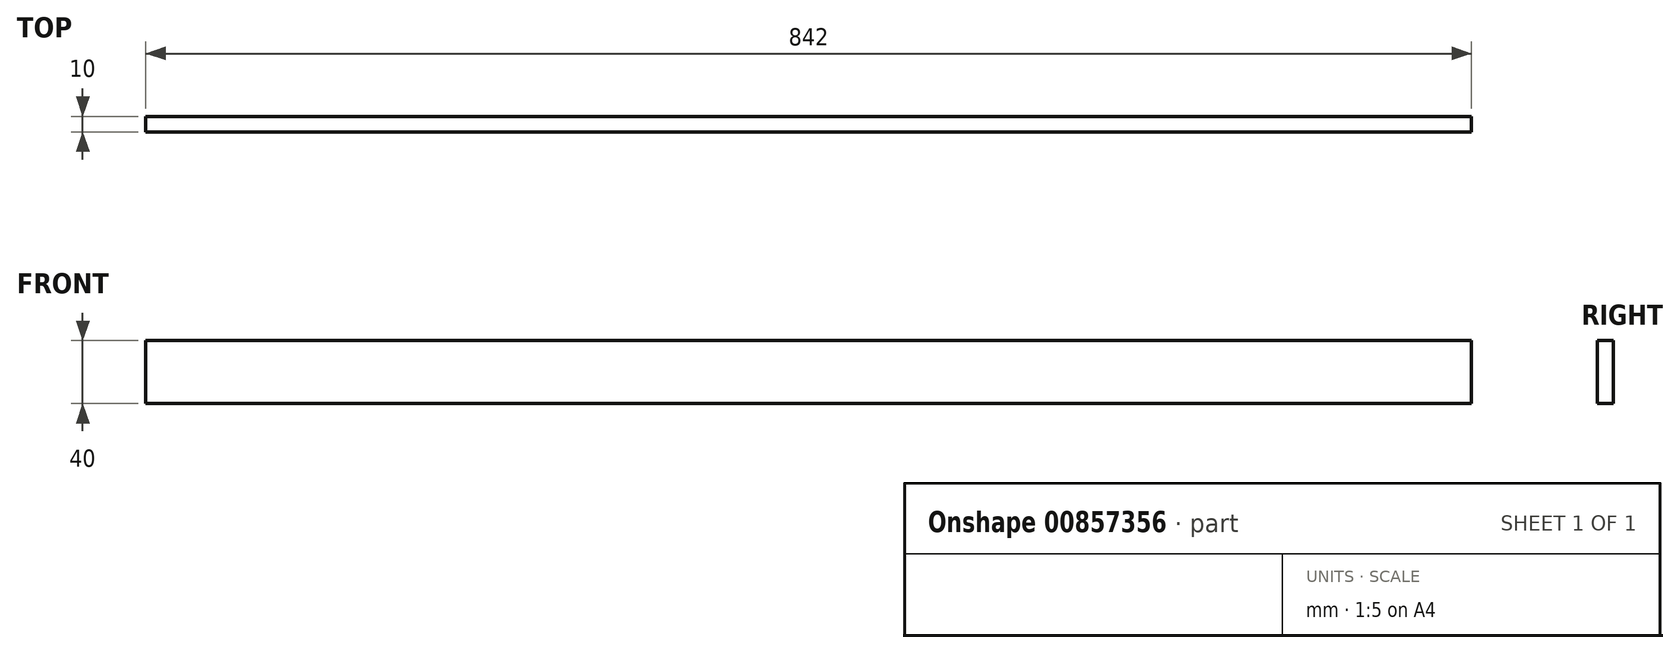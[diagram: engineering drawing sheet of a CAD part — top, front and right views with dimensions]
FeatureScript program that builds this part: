
annotation { "Feature Type Name" : "Feature", "Feature Type Description" : "" }
export const myFeature = defineFeature(function(context is Context, id is Id, definition is map)
    precondition{}
    {
        {
            var Q0;
            Q0=qCreatedBy(makeId("Right.planeOp"),FACE);
            var sketch = newSketch(context, id + "F0", { "sketchPlane" : qUnion([Q0])});
            skLineSegment(sketch, "E0.bottom", {"start": v(-6.46, 23.62) * mm, "end": v(3.54, 23.62) * mm});
            skLineSegment(sketch, "E0.top", {"start": v(-6.46, -16.38) * mm, "end": v(3.54, -16.38) * mm});
            skLineSegment(sketch, "E0.left", {"start": v(-6.46, 23.62) * mm, "end": v(-6.46, -16.38) * mm});
            skLineSegment(sketch, "E0.right", {"start": v(3.54, 23.62) * mm, "end": v(3.54, -16.38) * mm});
            skSolve(sketch);
        }
        {
            var Q0;
            Q0=makeQuery(id+"F0.imprint","IMPRINT",FACE,{"disambiguationData":[TD([[makeQuery(id+"F0.imprint","IMPRINT",EDGE,{"derivedFrom":sQuery(id+"F0.wireOp",EDGE,"E0.bottom")}),-1.0]])]});
            extrude(context, id + "F1", {"entities" : qUnion([Q0]), "depth" : 842 * mm, "offsetDistance" : 25 * mm});
        }
    });
